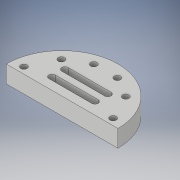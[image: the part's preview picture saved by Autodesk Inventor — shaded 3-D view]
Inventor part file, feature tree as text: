
AUTODESK INVENTOR PART (.ipt)
format: ipt  version: 2019 (Build 230136000, 136)  size: 147,456 bytes
history: native  units: mm
features: extrude x2, sketch x2
ambient origin geometry x8: Origin, YZ Plane, XZ Plane, XY Plane, X Axis, Y Axis, Z Axis, Center Point
bodies: Solid1 (feature_tree)
feature tree (4):
  extrude  "Extrusion1"  Depth=25.9969mm
  extrude  "Extrusion2"  Depth=3.0mm
  sketch  "Sketch1"  dims[d0=51.9938mm d1=25.9969mm]
  sketch  "Sketch2"  dims[d2=8.0mm d3=0.0mm d4=3.0mm d5=5.0mm d6=12.0mm d12=15.0mm d13=0.0mm d15=3.0mm d16=3.0mm d17=3.0mm d18=3.0mm d19=3.0mm d21=3.0mm d22=11.0mm d23=30.0mm d24=3.0mm d25=3.0mm d26=3.0mm d27=4.0mm d28=20.0mm]
